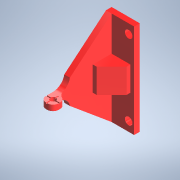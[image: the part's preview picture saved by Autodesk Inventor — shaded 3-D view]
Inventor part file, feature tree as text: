
AUTODESK INVENTOR PART (.ipt)
format: ipt  version: 2022 (Build 260153000, 153)  size: 216,576 bytes
history: native  units: mm
features: extrude x7, sketch x7, other x4, fillet x3, reference x2, chamfer x1, projected_geometry x1
ambient origin geometry x8: Origin, YZ Plane, XZ Plane, XY Plane, X Axis, Y Axis, Z Axis, Center Point
bodies: Body1 (feature_tree)
feature tree (25):
  other  "Твердое тело1"
  extrude  "Выдавливание1"  Depth=15.0mm
  extrude  "Выдавливание2"  Depth=50.0mm
  extrude  "Выдавливание3"  Depth=40.0mm
  fillet  "Сопряжение1"  Radius=5.0mm
  fillet  "Сопряжение2"  Radius=3.0mm
  extrude  "Выдавливание4"  Depth=35.0mm
  extrude  "Выдавливание5"  Depth=30.0mm
  extrude  "Выдавливание6"  Depth=1.5mm
  fillet  "Сопряжение3"  Radius=1.5mm
  extrude  "Выдавливание7"  Depth=3.0mm TaperAngle=0.0deg
  chamfer  "Фаска1"  Distance=3.0mm
  sketch  "Эскиз1"
  reference  "Ссылка1"
  reference  "Ссылка2"
  sketch  "Эскиз2"
  sketch  "Эскиз3"
  sketch  "Эскиз4"
  projected_geometry  "Спроецированная петля1"
  sketch  "Эскиз5"
  sketch  "Эскиз6"
  sketch  "Эскиз7"
  other  "<path> - Robot.iam"
  other  "000.000 - Robot.iam"
  other  "rpi3-bottom:1"
note: 1 file-system path scrubbed to <path> (originals preserved in map.json)
